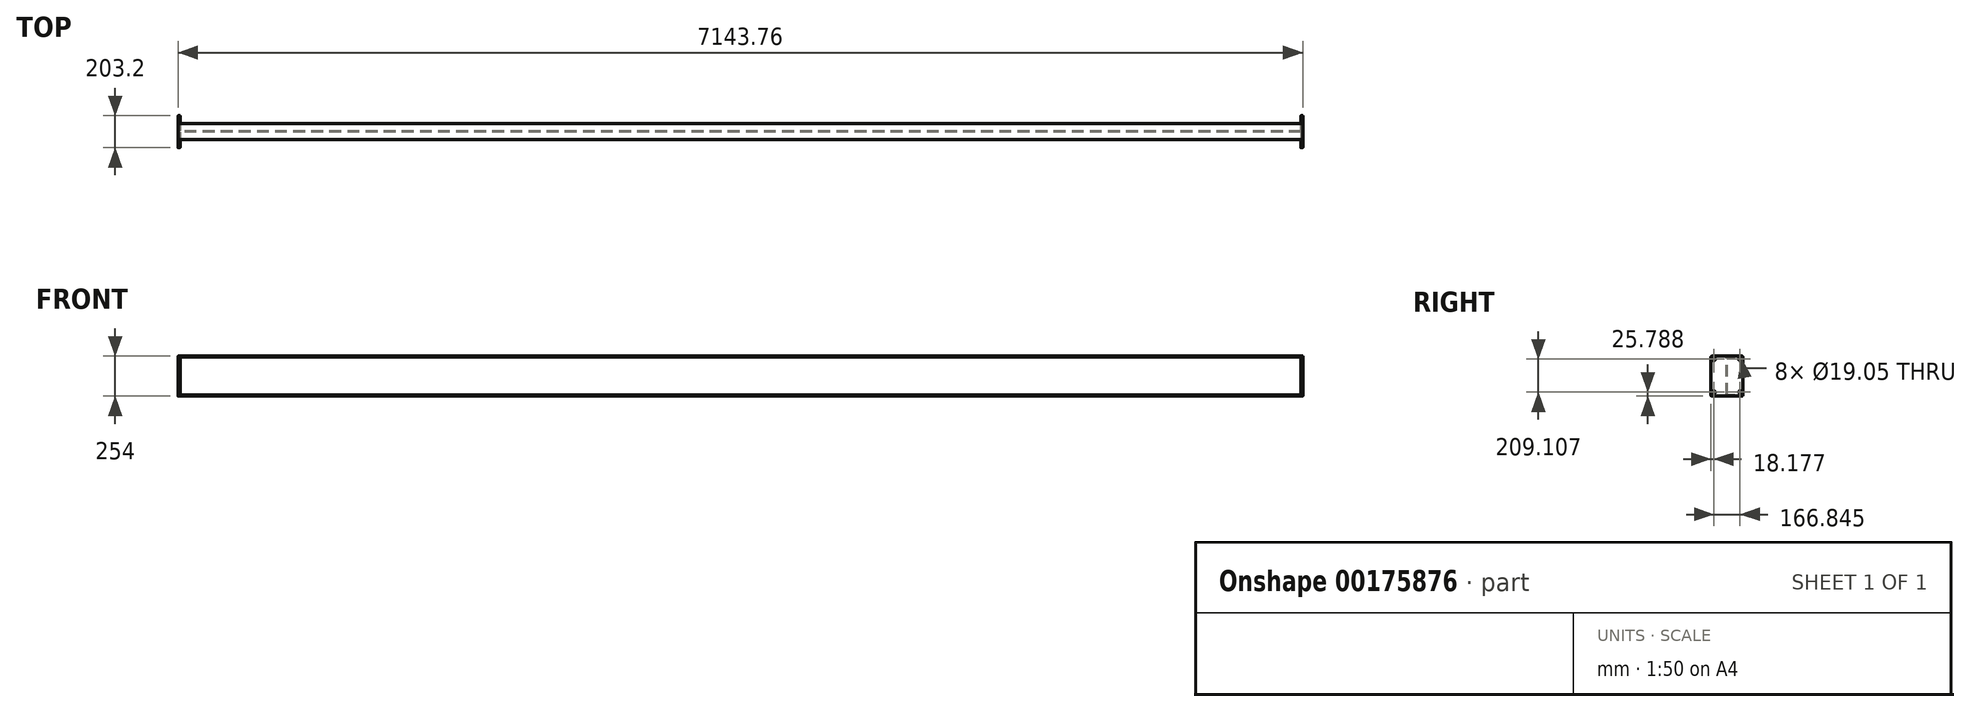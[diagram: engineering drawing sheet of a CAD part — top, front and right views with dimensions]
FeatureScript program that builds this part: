
annotation { "Feature Type Name" : "Feature", "Feature Type Description" : "" }
export const myFeature = defineFeature(function(context is Context, id is Id, definition is map)
    precondition{}
    {
        {
            var Q0;
            Q0=qCreatedBy(makeId("Right.planeOp"),FACE);
            var sketch = newSketch(context, id + "F0", { "sketchPlane" : qUnion([Q0])});
            skLineSegment(sketch, "E0", {"start": v(0, 0) * mm, "end": v(-50.8, 0) * mm});
            skLineSegment(sketch, "E1", {"start": v(-50.8, 0) * mm, "end": v(-50.8, 6.35) * mm});
            skLineSegment(sketch, "E2", {"start": v(-50.8, 6.35) * mm, "end": v(-6.22, 6.35) * mm});
            skLineSegment(sketch, "E3", {"start": v(-3.05, 9.53) * mm, "end": v(-3.05, 244.47) * mm});
            skLineSegment(sketch, "E4", {"start": v(-6.22, 247.65) * mm, "end": v(-50.8, 247.65) * mm});
            skLineSegment(sketch, "E5", {"start": v(-50.8, 247.65) * mm, "end": v(-50.8, 254) * mm});
            skLineSegment(sketch, "E6", {"start": v(-50.8, 254) * mm, "end": v(0, 254) * mm});
            skLineSegment(sketch, "E7.MirrorCS", {"start": v(50.8, 247.65) * mm, "end": v(50.8, 254) * mm});
            skLineSegment(sketch, "E8.MirrorCS", {"start": v(50.8, 0) * mm, "end": v(50.8, 6.35) * mm});
            skLineSegment(sketch, "E9.MirrorCS", {"start": v(50.8, 254) * mm, "end": v(0, 254) * mm});
            skLineSegment(sketch, "E10.MirrorCS", {"start": v(50.8, 6.35) * mm, "end": v(6.22, 6.35) * mm});
            skLineSegment(sketch, "E11.MirrorCS", {"start": v(0, 0) * mm, "end": v(50.8, 0) * mm});
            skLineSegment(sketch, "E12.MirrorCS", {"start": v(3.05, 247.65) * mm, "end": v(50.8, 247.65) * mm});
            skLineSegment(sketch, "E13.MirrorCS", {"start": v(3.05, 9.52) * mm, "end": v(3.05, 247.65) * mm});
            skPoint(sketch, "E14.visualSharp", {"position": v(-3.05, 247.65) * mm});
            skArc(sketch, "E14.filletArc", {"start": v(-3.05, 244.47) * mm, "mid": v(-3.98, 246.72) * mm, "end": v(-6.22, 247.65) * mm});
            skPoint(sketch, "E15.visualSharp", {"position": v(3.05, 6.35) * mm});
            skArc(sketch, "E15.filletArc", {"start": v(3.05, 9.52) * mm, "mid": v(3.98, 7.28) * mm, "end": v(6.22, 6.35) * mm});
            skPoint(sketch, "E16.visualSharp", {"position": v(-3.05, 6.35) * mm});
            skArc(sketch, "E16.filletArc", {"start": v(-6.22, 6.35) * mm, "mid": v(-3.98, 7.28) * mm, "end": v(-3.05, 9.53) * mm});
            skSolve(sketch);
        }
        {
            var Q0;
            Q0 = qSketchRegion(id + "F0", true);
            extrude(context, id + "F1", {"entities" : qUnion([Q0]), "endBound" : BoundingType.SYMMETRIC, "depth" : 7118.35 * mm});
        }
        {
            var Q0;
            Q0=makeQuery(id+"F1.opExtrude","CAP_FACE",FACE,{"disambiguationData":[OSD([sQuery(id+"F0.wireOp",EDGE,"E0"),sQuery(id+"F0.wireOp",EDGE,"E1"),sQuery(id+"F0.wireOp",EDGE,"E2"),sQuery(id+"F0.wireOp",EDGE,"E3"),sQuery(id+"F0.wireOp",EDGE,"E4"),sQuery(id+"F0.wireOp",EDGE,"E5"),sQuery(id+"F0.wireOp",EDGE,"E6"),sQuery(id+"F0.wireOp",EDGE,"E7.MirrorCS"),sQuery(id+"F0.wireOp",EDGE,"E8.MirrorCS"),sQuery(id+"F0.wireOp",EDGE,"E9.MirrorCS"),sQuery(id+"F0.wireOp",EDGE,"E10.MirrorCS"),sQuery(id+"F0.wireOp",EDGE,"E11.MirrorCS"),sQuery(id+"F0.wireOp",EDGE,"E12.MirrorCS"),sQuery(id+"F0.wireOp",EDGE,"E13.MirrorCS"),sQuery(id+"F0.wireOp",EDGE,"E14.filletArc"),sQuery(id+"F0.wireOp",EDGE,"E15.filletArc"),sQuery(id+"F0.wireOp",EDGE,"E16.filletArc")])],"isStart":false});
            var sketch = newSketch(context, id + "F2", { "sketchPlane" : qUnion([Q0])});
            skLineSegment(sketch, "E17.bottom", {"start": v(95.25, 254) * mm, "end": v(-95.25, 254) * mm});
            skLineSegment(sketch, "E17.top", {"start": v(95.25, 0) * mm, "end": v(-95.25, 0) * mm});
            skLineSegment(sketch, "E17.left", {"start": v(101.6, 247.65) * mm, "end": v(101.6, 6.35) * mm});
            skLineSegment(sketch, "E17.right", {"start": v(-101.6, 247.65) * mm, "end": v(-101.6, 6.35) * mm});
            skPoint(sketch, "E17.middle", {"position": v(0, 127) * mm});
            skPoint(sketch, "E18", {"position": v(-3.05, 127) * mm});
            skPoint(sketch, "E19.visualSharp", {"position": v(-101.6, 254) * mm});
            skArc(sketch, "E19.filletArc", {"start": v(-95.25, 254) * mm, "mid": v(-99.74, 252.14) * mm, "end": v(-101.6, 247.65) * mm});
            skPoint(sketch, "E20.visualSharp", {"position": v(101.6, 254) * mm});
            skArc(sketch, "E20.filletArc", {"start": v(101.6, 247.65) * mm, "mid": v(99.74, 252.14) * mm, "end": v(95.25, 254) * mm});
            skPoint(sketch, "E21.visualSharp", {"position": v(101.6, 0) * mm});
            skArc(sketch, "E21.filletArc", {"start": v(95.25, 0) * mm, "mid": v(99.74, 1.86) * mm, "end": v(101.6, 6.35) * mm});
            skPoint(sketch, "E22.visualSharp", {"position": v(-101.6, 0) * mm});
            skArc(sketch, "E22.filletArc", {"start": v(-101.6, 6.35) * mm, "mid": v(-99.74, 1.86) * mm, "end": v(-95.25, 0) * mm});
            skCircle(sketch, "E23", {"center": v(83.42, 234.9) * mm, "radius": 9.53 * mm});
            skCircle(sketch, "E24", {"center": v(83.42, 25.79) * mm, "radius": 9.53 * mm});
            skCircle(sketch, "E25.MirrorC", {"center": v(-83.42, 234.9) * mm, "radius": 9.53 * mm});
            skCircle(sketch, "E26.MirrorC", {"center": v(-83.42, 25.79) * mm, "radius": 9.53 * mm});
            skSolve(sketch);
        }
        {
            var Q0;
            Q0 = qSketchRegion(id + "F2", true);
            extrude(context, id + "F3", {"entities" : qUnion([Q0]), "depth" : 12.7 * mm});
        }
        {
            var Q0;
            Q0=makeQuery(id+"F3.opExtrude","SWEPT_BODY",BODY,{"disambiguationData":[OSD([sQuery(id+"F2.wireOp",EDGE,"E17.bottom"),sQuery(id+"F2.wireOp",EDGE,"E17.top"),sQuery(id+"F2.wireOp",EDGE,"E17.left"),sQuery(id+"F2.wireOp",EDGE,"E17.right"),sQuery(id+"F2.wireOp",EDGE,"E19.filletArc"),sQuery(id+"F2.wireOp",EDGE,"E20.filletArc"),sQuery(id+"F2.wireOp",EDGE,"E21.filletArc"),sQuery(id+"F2.wireOp",EDGE,"E22.filletArc"),sQuery(id+"F2.wireOp",EDGE,"E23"),sQuery(id+"F2.wireOp",EDGE,"E24"),sQuery(id+"F2.wireOp",EDGE,"E25.MirrorC"),sQuery(id+"F2.wireOp",EDGE,"E26.MirrorC")])]});
            var Q1;
            Q1=qCreatedBy(makeId("Right.planeOp"),FACE);
            mirror(context, id + "F4", {"operationType" : NewBodyOperationType.ADD, "entities" : qUnion([Q0]), "mirrorPlane" : qUnion([Q1])});
        }
    });
